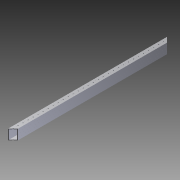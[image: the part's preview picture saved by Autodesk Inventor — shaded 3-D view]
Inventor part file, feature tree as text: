
AUTODESK INVENTOR PART (.ipt)
format: ipt  version: 2015 (Build 190159000, 159)  size: 754,688 bytes
history: native  units: in
note: dims shown in document units (in); Inventor stores cm internally (conversion verified against a paired STEP export)
features: other x2, extrude x2, sketch x2, imported_body x1
ambient origin geometry x8: Origin, YZ Plane, XZ Plane, XY Plane, X Axis, Y Axis, Z Axis, Center Point
bodies: Body1 (feature_tree)
feature tree (7):
  other  "Cut-Extrude2"
  other  "217-3453-STEP1"
  extrude  "Extrusion1"  Depth=31.667in
  extrude  "Extrusion2"  Depth=2.0in TaperAngle=0.0deg
  imported_body  "Base1"
  sketch  "Sketch1"  dims[d0=0.3092in d1=31.667in]
  sketch  "Sketch2"  dims[d2=0.3092in d3=2.0in d4=0.0in d5=31.667in d6=0.3092in d7=2.0in d8=0.0in]
